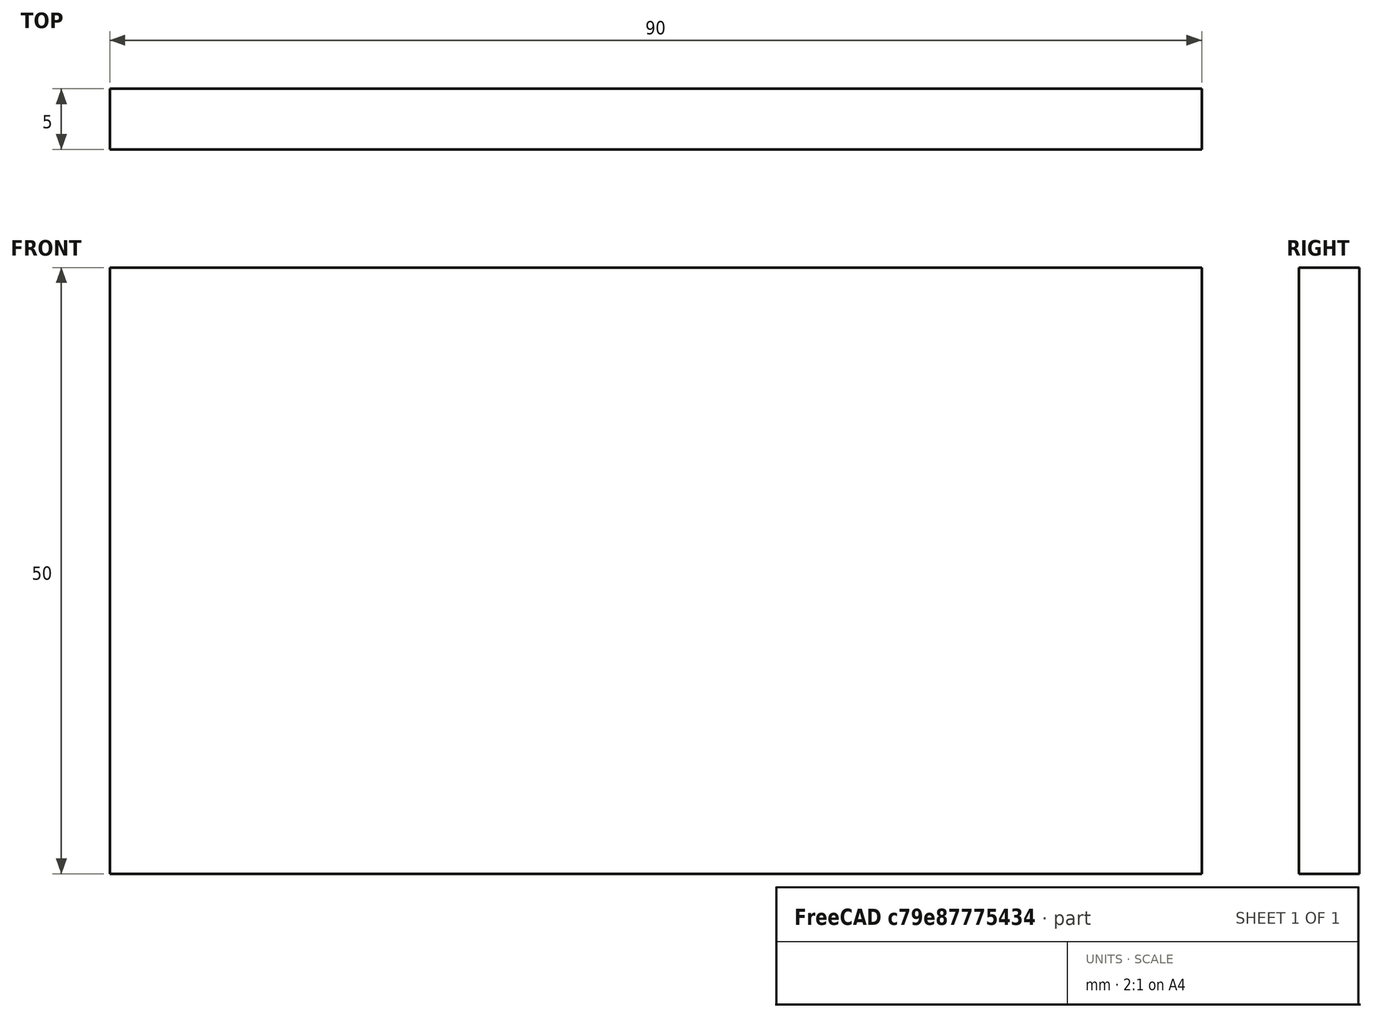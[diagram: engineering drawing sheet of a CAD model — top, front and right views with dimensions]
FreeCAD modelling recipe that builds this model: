
FCSTD DOCUMENT  (FreeCAD 0.15R4671 (Git))
Label: Flat Bar 90x5 EN10058 S235JR
License: All rights reserved
LicenseURL: http://en.wikipedia.org/wiki/All_rights_reserved
objects: Sketcher::SketchObject×1, Part::Extrusion×1
note: 2 computed .brp shape members not serialized (recipe doc carries the construction recipe); baked Part::Feature solids carry a one-line shape summary decoded from their .brp

FEATURE [Sketcher::SketchObject] Sketch
  sketch-geometry (4):
    g0: LineSegment StartX=-45 StartY=-2.5 StartZ=0 EndX=45 EndY=-2.5 EndZ=0
    g1: LineSegment StartX=45 StartY=-2.5 StartZ=0 EndX=45 EndY=2.5 EndZ=0
    g2: LineSegment StartX=45 StartY=2.5 StartZ=0 EndX=-45 EndY=2.5 EndZ=0
    g3: LineSegment StartX=-45 StartY=2.5 StartZ=0 EndX=-45 EndY=-2.5 EndZ=0
  constraints (12):
    c: Coincident(g0,g1)
    c: Coincident(g1,g2)
    c: Coincident(g2,g3)
    c: Coincident(g3,g0)
    c: Horizontal(g0)
    c: Horizontal(g2)
    c: Vertical(g1)
    c: Vertical(g3)
    c: Symmetric(g1,g2,g-2)
    c: Symmetric(g0,g1,g-1)
    c: DistanceY(g1) = 5
    c: DistanceX(g0) = 90
FEATURE [Part::Extrusion] Extrude  label="Flat Bar 90x5 EN10058 S235JR"
  Base = -> Sketch
  Dir = (0,0,50)
  Solid = true
